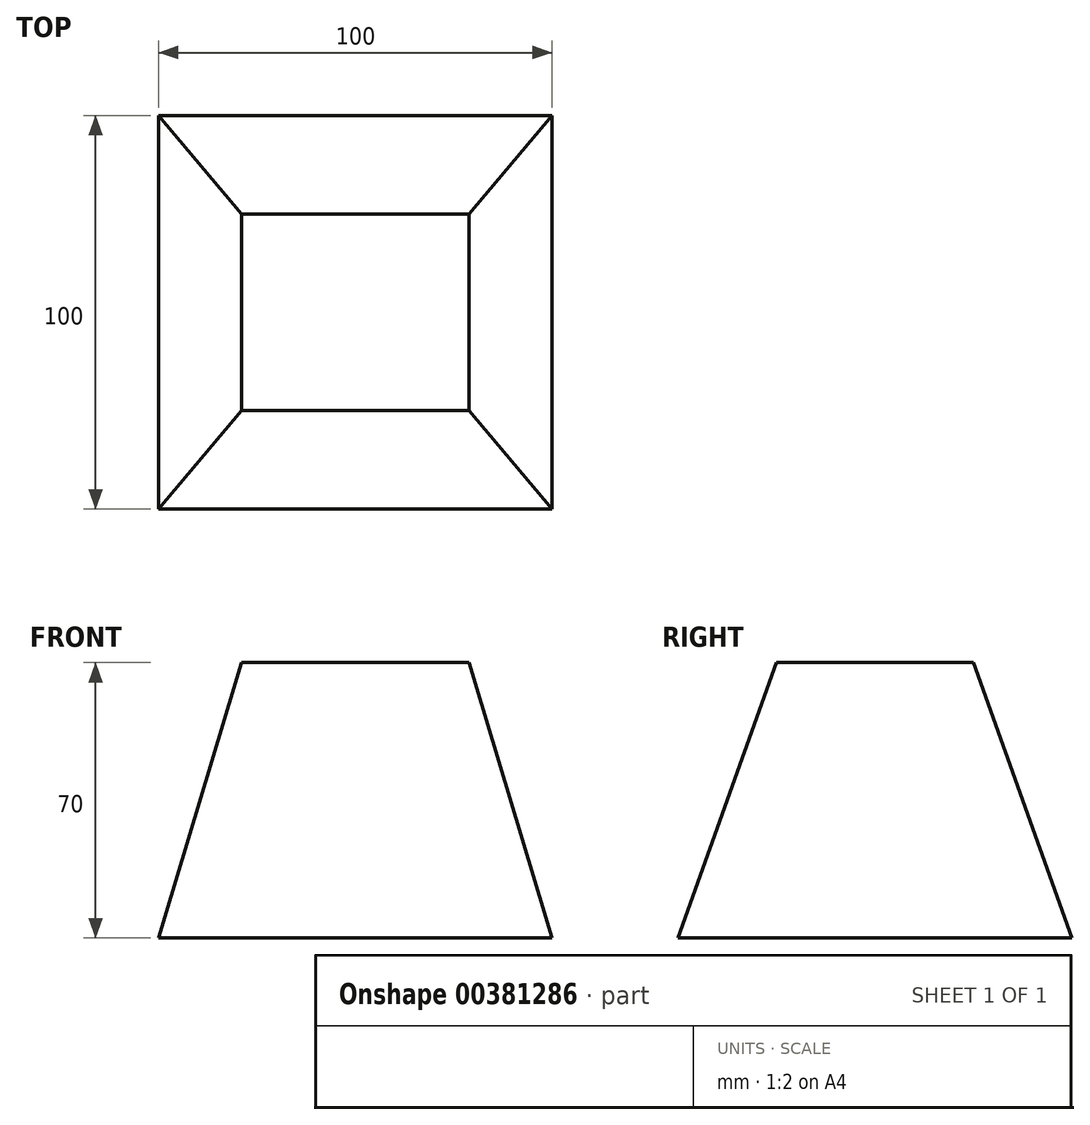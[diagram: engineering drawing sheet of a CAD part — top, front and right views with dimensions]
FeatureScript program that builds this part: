
annotation { "Feature Type Name" : "Feature", "Feature Type Description" : "" }
export const myFeature = defineFeature(function(context is Context, id is Id, definition is map)
    precondition{}
    {
        {
            var Q0;
            Q0=qCreatedBy(makeId("Top.planeOp"),FACE);
            cPlane(context, id + "F0", {"entities" : qUnion([Q0]), "cplaneType" : CPlaneType.OFFSET, "offset" : 70 * mm, "width" : 150 * mm, "height" : 150 * mm});
        }
        {
            var Q0;
            Q0=qCreatedBy(id+"F0.planeOp",FACE);
            var sketch = newSketch(context, id + "F1", { "sketchPlane" : qUnion([Q0])});
            skCircle(sketch, "E0.cCircle", {"center": v(0, 0) * mm, "radius": 25 * mm, "construction": true});
            skLineSegment(sketch, "E0.0", {"start": v(-14.43, 25) * mm, "end": v(14.43, 25) * mm});
            skLineSegment(sketch, "E0.1", {"start": v(14.43, 25) * mm, "end": v(28.87, 0) * mm});
            skLineSegment(sketch, "E0.2", {"start": v(28.87, 0) * mm, "end": v(14.43, -25) * mm});
            skLineSegment(sketch, "E0.3", {"start": v(14.43, -25) * mm, "end": v(-14.43, -25) * mm});
            skLineSegment(sketch, "E0.4", {"start": v(-14.43, -25) * mm, "end": v(-28.87, 0) * mm});
            skLineSegment(sketch, "E0.5", {"start": v(-28.87, 0) * mm, "end": v(-14.43, 25) * mm});
            skPoint(sketch, "E0.0.midPoint", {"position": v(0, 25) * mm});
            skSolve(sketch);
        }
        {
            var Q0;
            Q0=qCreatedBy(makeId("Top.planeOp"),FACE);
            var sketch = newSketch(context, id + "F2", { "sketchPlane" : qUnion([Q0])});
            skLineSegment(sketch, "E1.bottom", {"start": v(50, 50) * mm, "end": v(-50, 50) * mm});
            skLineSegment(sketch, "E1.top", {"start": v(50, -50) * mm, "end": v(-50, -50) * mm});
            skLineSegment(sketch, "E1.left", {"start": v(50, 50) * mm, "end": v(50, -50) * mm});
            skLineSegment(sketch, "E1.right", {"start": v(-50, 50) * mm, "end": v(-50, -50) * mm});
            skPoint(sketch, "E1.middle", {"position": v(0, 0) * mm});
            skSolve(sketch);
        }
        {
            var Q0;
            Q0=qCreatedBy(id+"F0.planeOp",FACE);
            var sketch = newSketch(context, id + "F3", { "sketchPlane" : qUnion([Q0])});
            skLineSegment(sketch, "E2.bottom", {"start": v(28.87, 25) * mm, "end": v(-28.87, 25) * mm});
            skLineSegment(sketch, "E2.top", {"start": v(28.87, -25) * mm, "end": v(-28.87, -25) * mm});
            skLineSegment(sketch, "E2.left", {"start": v(28.87, 25) * mm, "end": v(28.87, -25) * mm});
            skLineSegment(sketch, "E2.right", {"start": v(-28.87, 25) * mm, "end": v(-28.87, -25) * mm});
            skPoint(sketch, "E2.middle", {"position": v(0, 0) * mm});
            skSolve(sketch);
        }
        {
            var Q0;
            Q0=makeQuery(id+"F3.imprint","IMPRINT",FACE,{"disambiguationData":[TD([[makeQuery(id+"F3.imprint","IMPRINT",EDGE,{"derivedFrom":sQuery(id+"F3.wireOp",EDGE,"E2.bottom")}),1.0]])]});
            var Q1;
            Q1=makeQuery(id+"F2.imprint","IMPRINT",FACE,{"disambiguationData":[TD([[makeQuery(id+"F2.imprint","IMPRINT",EDGE,{"derivedFrom":sQuery(id+"F2.wireOp",EDGE,"E1.bottom")}),1.0]])]});
            loft(context, id + "F4", {"sheetProfilesArray" : [{ "sheetProfileEntities" : qUnion([Q0]) }, { "sheetProfileEntities" : qUnion([Q1]) }]});
        }
    });
